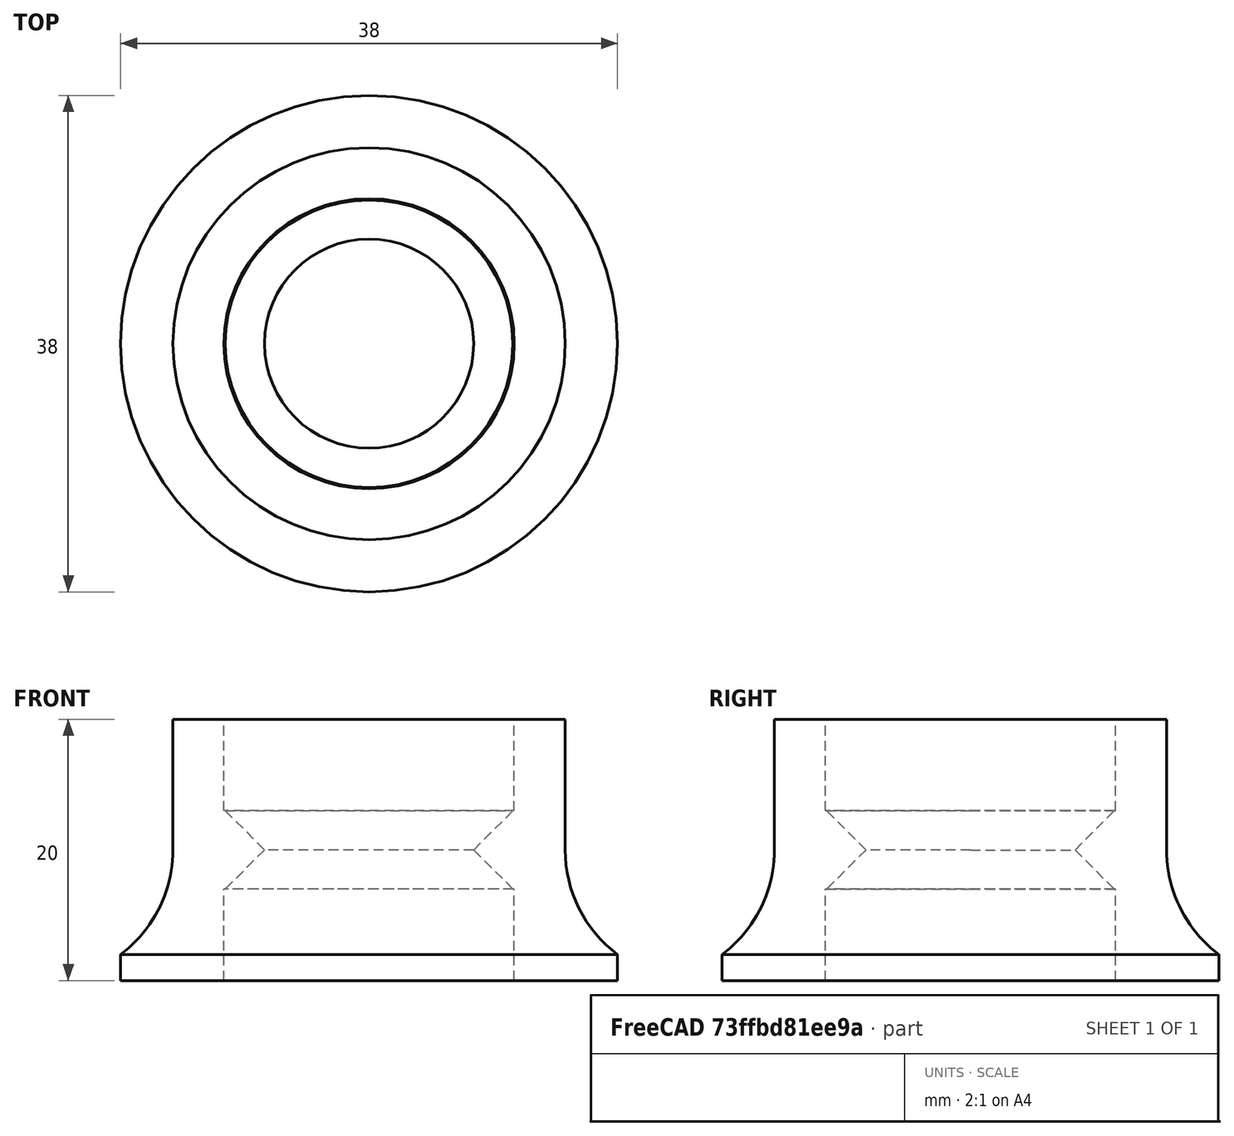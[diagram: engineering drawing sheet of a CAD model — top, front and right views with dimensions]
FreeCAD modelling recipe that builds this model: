
FCSTD DOCUMENT  (FreeCAD 0.17R13522 (Git))
Label: wheel
License: All rights reserved
LicenseURL: http://en.wikipedia.org/wiki/All_rights_reserved
objects: Part::Cylinder×4, Part::Cone×2, Part::MultiFuse×2, Part::Torus×1, Part::Cut×1
note: 10 computed .brp shape members not serialized (recipe doc carries the construction recipe); baked Part::Feature solids carry a one-line shape summary decoded from their .brp

FEATURE [Part::Cylinder] Cylinder001
  Angle = 360
  AttacherType = Attacher::AttachEngine3D
  Height = 7
  Radius = 11.1
FEATURE [Part::Cylinder] Cylinder002
  Angle = 360
  AttacherType = Attacher::AttachEngine3D
  Height = 7
  Placement = pos=(0,0,13) rot=(0,0,1;0rad)
  Radius = 11.1
FEATURE [Part::Cone] Cone
  Angle = 360
  AttacherType = Attacher::AttachEngine3D
  Height = 11
  Placement = pos=(0,0,7) rot=(0,0,1;0rad)
  Radius1 = 11
  Radius2 = 0
FEATURE [Part::Cone] Cone001
  Angle = 360
  AttacherType = Attacher::AttachEngine3D
  Height = 11
  Placement = pos=(0,0,13) rot=(0,1,0;3.14159rad)
  Radius1 = 11
  Radius2 = 0
FEATURE [Part::Torus] Torus002
  Angle1 = -180
  Angle2 = 180
  Angle3 = 360
  AttacherType = Attacher::AttachEngine3D
  Placement = pos=(0,0,10) rot=(0,0,1;0rad)
  Radius1 = 25
  Radius2 = 10
FEATURE [Part::MultiFuse] Fusion  label="NegativeFusion"
  Shapes = -> [Cylinder001,Cylinder002,Cone,Cone001,Torus002]
FEATURE [Part::Cylinder] Cylinder003
  Angle = 360
  AttacherType = Attacher::AttachEngine3D
  Height = 10
  Radius = 19
FEATURE [Part::Cylinder] Cylinder
  Angle = 360
  AttacherType = Attacher::AttachEngine3D
  Height = 20
  Radius = 15
FEATURE [Part::MultiFuse] Fusion001  label="Positive Fusion"
  Shapes = -> [Cylinder003,Cylinder]
FEATURE [Part::Cut] Cut
  Base = -> Fusion001
  Tool = -> Fusion
